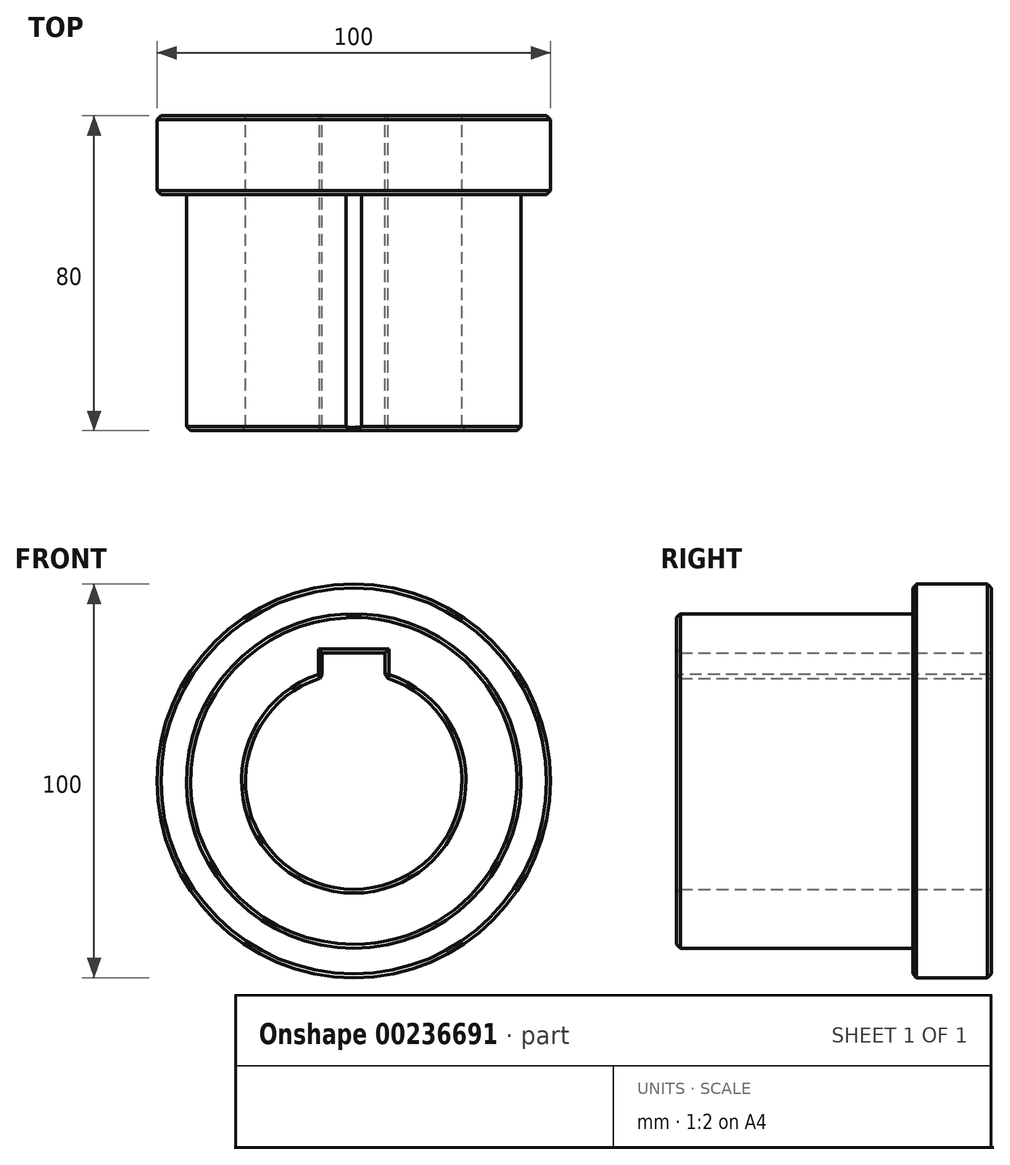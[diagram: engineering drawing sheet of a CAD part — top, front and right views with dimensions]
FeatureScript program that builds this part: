
annotation { "Feature Type Name" : "Feature", "Feature Type Description" : "" }
export const myFeature = defineFeature(function(context is Context, id is Id, definition is map)
    precondition{}
    {
        {
            var Q0;
            Q0=qCreatedBy(makeId("Front.planeOp"),FACE);
            var sketch = newSketch(context, id + "F0", { "sketchPlane" : qUnion([Q0])});
            skCircle(sketch, "E0", {"center": v(0, 0) * mm, "radius": 42.5 * mm});
            skSolve(sketch);
        }
        {
            var Q0;
            Q0 = qSketchRegion(id + "F0", true);
            extrude(context, id + "F1", {"entities" : qUnion([Q0]), "depth" : 60 * mm, "offsetDistance" : 25 * mm});
        }
        {
            var Q0;
            Q0=makeQuery(id+"F1.opExtrude","CAP_FACE",FACE,{"disambiguationData":[OSD([sQuery(id+"F0.wireOp",EDGE,"E0")])],"isStart":true});
            var sketch = newSketch(context, id + "F2", { "sketchPlane" : qUnion([Q0])});
            skCircle(sketch, "E1", {"center": v(0, 0) * mm, "radius": 50 * mm});
            skSolve(sketch);
        }
        {
            var Q0;
            Q0 = qSketchRegion(id + "F2", true);
            extrude(context, id + "F3", {"entities" : qUnion([Q0]), "operationType" : NewBodyOperationType.ADD, "depth" : 20 * mm, "offsetDistance" : 25 * mm});
        }
        {
            var Q0;
            Q0=makeQuery(id+"F3.opExtrude","CAP_FACE",FACE,{"disambiguationData":[OSD([sQuery(id+"F2.wireOp",EDGE,"E1")])],"isStart":false});
            var sketch = newSketch(context, id + "F4", { "sketchPlane" : qUnion([Q0])});
            skArc(sketch, "E2", {"start": v(-8, 26.31) * mm, "mid": v(0, -27.5) * mm, "end": v(8, 26.31) * mm});
            skLineSegment(sketch, "E3.bottom", {"start": v(-8, 32.5) * mm, "end": v(8, 32.5) * mm});
            skLineSegment(sketch, "E3.left", {"start": v(-8, 32.5) * mm, "end": v(-8, 26.31) * mm});
            skLineSegment(sketch, "E3.right", {"start": v(8, 32.5) * mm, "end": v(8, 26.31) * mm});
            skSolve(sketch);
        }
        {
            var Q0;
            Q0 = qSketchRegion(id + "F4", true);
            extrude(context, id + "F5", {"entities" : qUnion([Q0]), "operationType" : NewBodyOperationType.REMOVE, "endBound" : BoundingType.THROUGH_ALL, "oppositeDirection" : true, "depth" : 25 * mm, "offsetDistance" : 25 * mm});
        }
        {
            var Q0;
            Q0=makeQuery(id+"F3.opExtrude","CAP_EDGE",EDGE,{"disambiguationData":[OSD([sQuery(id+"F2.wireOp",EDGE,"E1")])],"isStart":false});
            var Q1;
            Q1=makeQuery(id+"F5.boolean.opBoolean","COPY",EDGE,{"derivedFrom":makeQuery(id+"F5.opExtrude","CAP_EDGE",EDGE,{"disambiguationData":[OSD([sQuery(id+"F4.wireOp",EDGE,"E2")])],"isStart":true})});
            var Q2;
            Q2=makeQuery(id+"F5.boolean.opBoolean","COPY",EDGE,{"derivedFrom":makeQuery(id+"F5.opExtrude","CAP_EDGE",EDGE,{"disambiguationData":[OSD([sQuery(id+"F4.wireOp",EDGE,"E3.left")])],"isStart":true})});
            var Q3;
            Q3=makeQuery(id+"F5.boolean.opBoolean","COPY",EDGE,{"derivedFrom":makeQuery(id+"F5.opExtrude","CAP_EDGE",EDGE,{"disambiguationData":[OSD([sQuery(id+"F4.wireOp",EDGE,"E3.bottom")])],"isStart":true})});
            var Q4;
            Q4=makeQuery(id+"F5.boolean.opBoolean","COPY",EDGE,{"derivedFrom":makeQuery(id+"F5.opExtrude","CAP_EDGE",EDGE,{"disambiguationData":[OSD([sQuery(id+"F4.wireOp",EDGE,"E3.right")])],"isStart":true})});
            var Q5;
            Q5=makeQuery(id+"F1.opExtrude","CAP_EDGE",EDGE,{"disambiguationData":[OSD([sQuery(id+"F0.wireOp",EDGE,"E0")])],"isStart":false});
            var Q6;
            Q6=makeQuery(id+"F5.boolean.opBoolean","INTERSECT",EDGE,{"derivedFrom":[makeQuery(id+"F1.opExtrude","CAP_FACE",FACE,{"disambiguationData":[OSD([sQuery(id+"F0.wireOp",EDGE,"E0")])],"isStart":false}),makeQuery(id+"F5.opExtrude","SWEPT_FACE",FACE,{"disambiguationData":[OSD([sQuery(id+"F4.wireOp",EDGE,"E2")])]})]});
            var Q7;
            Q7=makeQuery(id+"F3.opExtrude","CAP_EDGE",EDGE,{"disambiguationData":[OSD([sQuery(id+"F2.wireOp",EDGE,"E1")])],"isStart":true});
            var Q8;
            Q8=makeQuery(id+"F5.boolean.opBoolean","INTERSECT",EDGE,{"derivedFrom":[makeQuery(id+"F1.opExtrude","CAP_FACE",FACE,{"disambiguationData":[OSD([sQuery(id+"F0.wireOp",EDGE,"E0")])],"isStart":false}),makeQuery(id+"F5.opExtrude","SWEPT_FACE",FACE,{"disambiguationData":[OSD([sQuery(id+"F4.wireOp",EDGE,"E3.bottom")])]})]});
            var Q9;
            Q9=makeQuery(id+"F5.boolean.opBoolean","INTERSECT",EDGE,{"derivedFrom":[makeQuery(id+"F1.opExtrude","CAP_FACE",FACE,{"disambiguationData":[OSD([sQuery(id+"F0.wireOp",EDGE,"E0")])],"isStart":false}),makeQuery(id+"F5.opExtrude","SWEPT_FACE",FACE,{"disambiguationData":[OSD([sQuery(id+"F4.wireOp",EDGE,"E3.left")])]})]});
            var Q10;
            Q10=makeQuery(id+"F5.boolean.opBoolean","INTERSECT",EDGE,{"derivedFrom":[makeQuery(id+"F1.opExtrude","CAP_FACE",FACE,{"disambiguationData":[OSD([sQuery(id+"F0.wireOp",EDGE,"E0")])],"isStart":false}),makeQuery(id+"F5.opExtrude","SWEPT_FACE",FACE,{"disambiguationData":[OSD([sQuery(id+"F4.wireOp",EDGE,"E3.right")])]})]});
            var Q11;
            Q11=makeQuery(id+"F5.boolean.opBoolean","COPY",EDGE,{"derivedFrom":makeQuery(id+"F5.opExtrude","SWEPT_EDGE",EDGE,{"disambiguationData":[OSD([sQuery(id+"F4.wireOp",EDGE,"E2"),sQuery(id+"F4.wireOp",EDGE,"E3.right")])]})});
            var Q12;
            Q12=makeQuery(id+"F5.boolean.opBoolean","COPY",EDGE,{"derivedFrom":makeQuery(id+"F5.opExtrude","SWEPT_EDGE",EDGE,{"disambiguationData":[OSD([sQuery(id+"F4.wireOp",EDGE,"E2"),sQuery(id+"F4.wireOp",EDGE,"E3.left")])]})});
            chamfer(context, id + "F6", {"entities" : qUnion([Q0, Q1, Q2, Q3, Q4, Q5, Q6, Q7, Q8, Q9, Q10, Q11, Q12]), "width" : 1 * mm, "tangentPropagation" : true});
        }
        {
            var Q0;
            Q0=makeQuery(id+"F1.opExtrude","CAP_FACE",FACE,{"disambiguationData":[OSD([sQuery(id+"F0.wireOp",EDGE,"E0")])],"isStart":false});
            var sketch = newSketch(context, id + "F7", { "sketchPlane" : qUnion([Q0])});
            skLineSegment(sketch, "E4.bottom", {"start": v(-2, 42.3) * mm, "end": v(2, 42.3) * mm});
            skLineSegment(sketch, "E4.top", {"start": v(-2, 46.78) * mm, "end": v(2, 46.78) * mm});
            skLineSegment(sketch, "E4.left", {"start": v(-2, 42.3) * mm, "end": v(-2, 46.78) * mm});
            skLineSegment(sketch, "E4.right", {"start": v(2, 42.3) * mm, "end": v(2, 46.78) * mm});
            skSolve(sketch);
        }
        {
            var Q0;
            Q0=makeQuery(id+"F7.imprint","IMPRINT",FACE,{"disambiguationData":[TD([[makeQuery(id+"F7.imprint","IMPRINT",EDGE,{"derivedFrom":sQuery(id+"F7.wireOp",EDGE,"E4.bottom")}),1.0]])]});
            var Q1;
            Q1=makeQuery(id+"F3.opExtrude","CAP_FACE",FACE,{"disambiguationData":[OSD([sQuery(id+"F2.wireOp",EDGE,"E1")])],"isStart":true});
            extrude(context, id + "F8", {"entities" : qUnion([Q0]), "operationType" : NewBodyOperationType.REMOVE, "endBound" : BoundingType.UP_TO_SURFACE, "oppositeDirection" : true, "depth" : 25 * mm, "endBoundEntityFace" : qUnion([Q1]), "offsetDistance" : 25 * mm});
        }
    });
